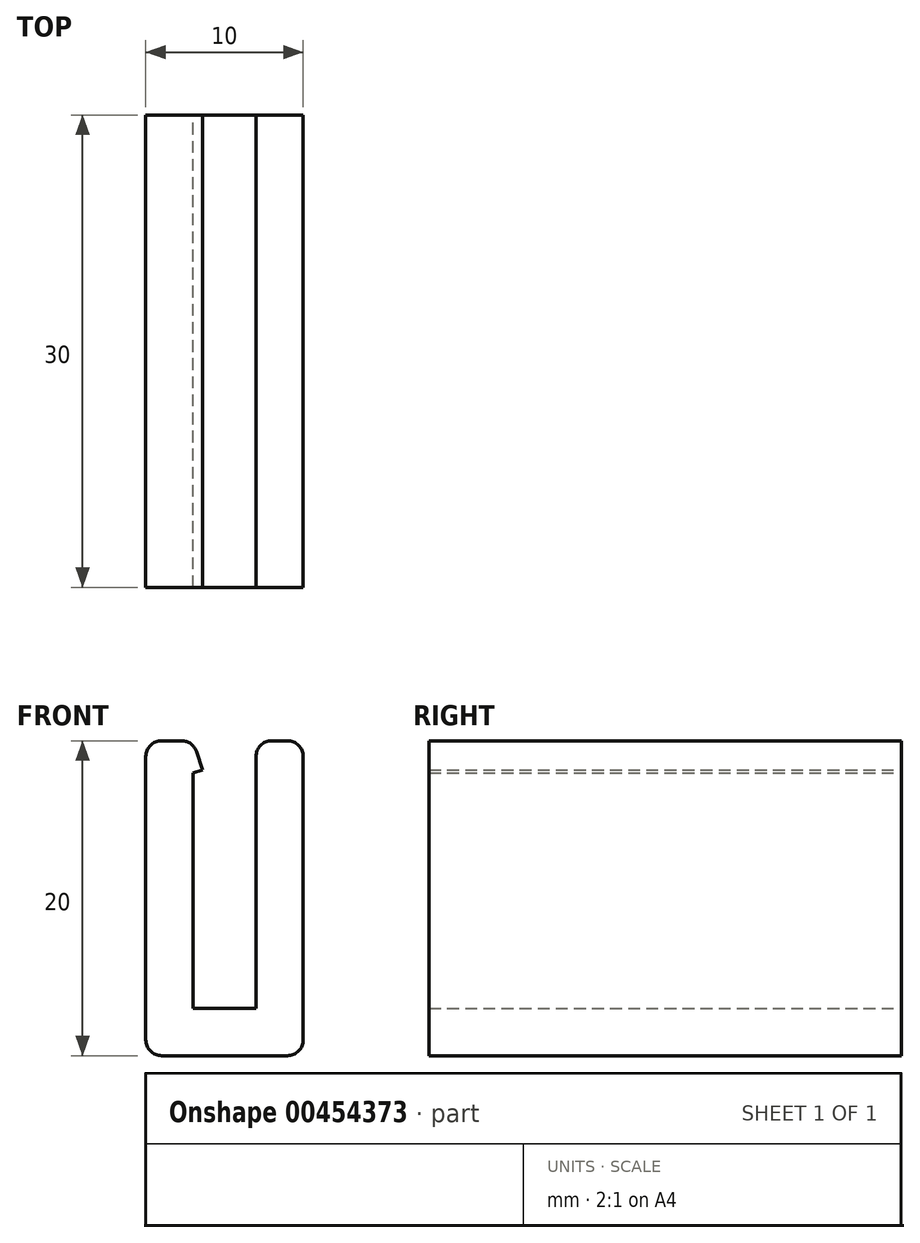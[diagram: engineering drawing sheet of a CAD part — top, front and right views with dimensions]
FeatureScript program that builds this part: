
annotation { "Feature Type Name" : "Feature", "Feature Type Description" : "" }
export const myFeature = defineFeature(function(context is Context, id is Id, definition is map)
    precondition{}
    {
        {
            var Q0;
            Q0=qCreatedBy(makeId("Front.planeOp"),FACE);
            var sketch = newSketch(context, id + "F0", { "sketchPlane" : qUnion([Q0])});
            skLineSegment(sketch, "E0", {"start": v(-44.17, 19.27) * mm, "end": v(-34.17, 19.27) * mm});
            skLineSegment(sketch, "E1", {"start": v(-34.17, 19.27) * mm, "end": v(-34.17, 39.27) * mm});
            skLineSegment(sketch, "E2", {"start": v(-44.17, 19.27) * mm, "end": v(-44.17, 39.27) * mm});
            skLineSegment(sketch, "E3.0", {"start": v(-41.17, 22.27) * mm, "end": v(-37.17, 22.27) * mm});
            skLineSegment(sketch, "E4.0", {"start": v(-37.17, 22.27) * mm, "end": v(-37.17, 39.27) * mm});
            skLineSegment(sketch, "E5.0", {"start": v(-41.17, 22.27) * mm, "end": v(-41.17, 37.23) * mm});
            skLineSegment(sketch, "E6", {"start": v(-37.17, 39.27) * mm, "end": v(-34.17, 39.27) * mm});
            skLineSegment(sketch, "E7", {"start": v(-44.17, 39.27) * mm, "end": v(-41.17, 39.27) * mm});
            skLineSegment(sketch, "E8", {"start": v(-41.17, 39.27) * mm, "end": v(-40.56, 37.43) * mm});
            skLineSegment(sketch, "E9", {"start": v(-40.56, 37.43) * mm, "end": v(-41.17, 37.23) * mm});
            skSolve(sketch);
        }
        {
            var Q0;
            Q0=makeQuery(id+"F0.imprint","IMPRINT",FACE,{"disambiguationData":[TD([[makeQuery(id+"F0.imprint","IMPRINT",EDGE,{"derivedFrom":sQuery(id+"F0.wireOp",EDGE,"E0")}),1.0]])]});
            extrude(context, id + "F1", {"entities" : qUnion([Q0]), "depth" : 30 * mm});
        }
        {
            var Q0;
            Q0=makeQuery(id+"F1.opExtrude","SWEPT_EDGE",EDGE,{"disambiguationData":[OSD([sQuery(id+"F0.wireOp",EDGE,"E0"),sQuery(id+"F0.wireOp",EDGE,"E1")])]});
            var Q1;
            Q1=makeQuery(id+"F1.opExtrude","SWEPT_EDGE",EDGE,{"disambiguationData":[OSD([sQuery(id+"F0.wireOp",EDGE,"E1"),sQuery(id+"F0.wireOp",EDGE,"E6")])]});
            var Q2;
            Q2=makeQuery(id+"F1.opExtrude","SWEPT_EDGE",EDGE,{"disambiguationData":[OSD([sQuery(id+"F0.wireOp",EDGE,"E4.0"),sQuery(id+"F0.wireOp",EDGE,"E6")])]});
            var Q3;
            Q3=makeQuery(id+"F1.opExtrude","SWEPT_EDGE",EDGE,{"disambiguationData":[OSD([sQuery(id+"F0.wireOp",EDGE,"E0"),sQuery(id+"F0.wireOp",EDGE,"E2")])]});
            var Q4;
            Q4=makeQuery(id+"F1.opExtrude","SWEPT_EDGE",EDGE,{"disambiguationData":[OSD([sQuery(id+"F0.wireOp",EDGE,"E2"),sQuery(id+"F0.wireOp",EDGE,"E7")])]});
            var Q5;
            Q5=makeQuery(id+"F1.opExtrude","SWEPT_EDGE",EDGE,{"disambiguationData":[OSD([sQuery(id+"F0.wireOp",EDGE,"E7"),sQuery(id+"F0.wireOp",EDGE,"E8")])]});
            fillet(context, id + "F2", {"entities" : qUnion([Q0, Q1, Q2, Q3, Q4, Q5]), "radius" : 1 * mm, "tangentPropagation" : true, "allowEdgeOverflow" : false});
        }
    });
